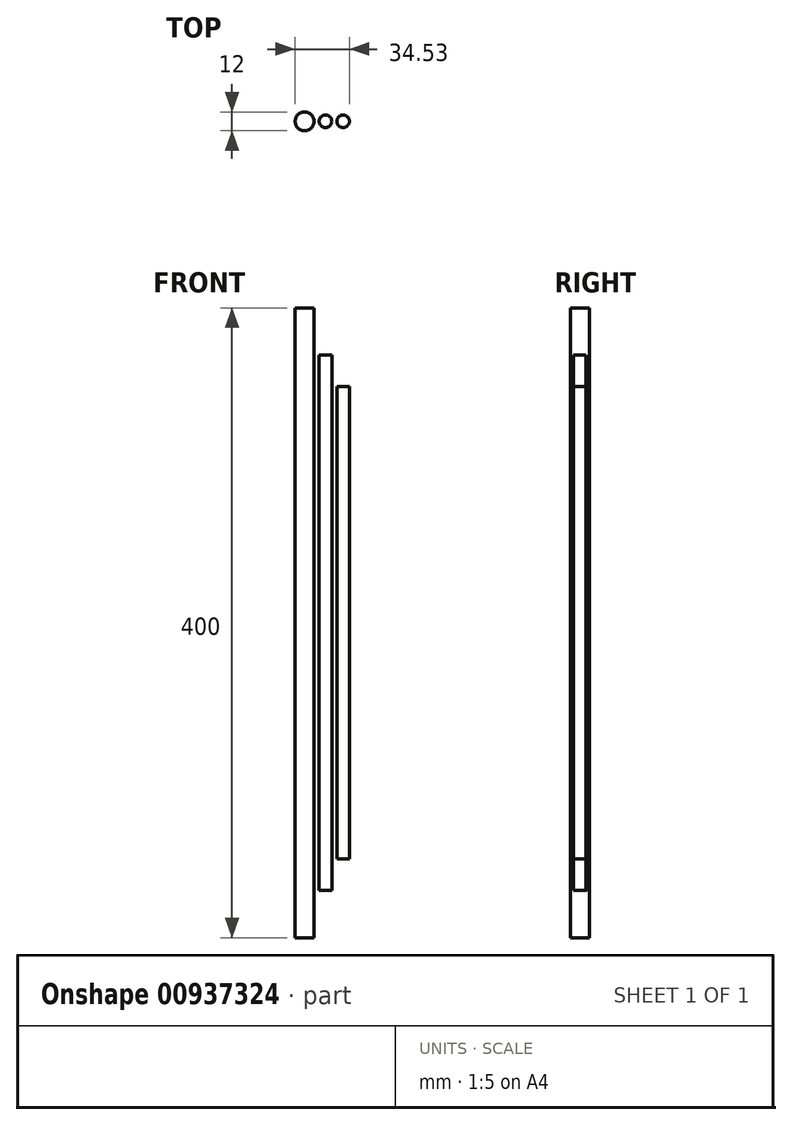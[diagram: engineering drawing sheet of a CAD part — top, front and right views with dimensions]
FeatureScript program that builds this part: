
annotation { "Feature Type Name" : "Feature", "Feature Type Description" : "" }
export const myFeature = defineFeature(function(context is Context, id is Id, definition is map)
    precondition{}
    {
        {
            var Q0;
            Q0=qCreatedBy(makeId("Top.planeOp"),FACE);
            var sketch = newSketch(context, id + "F0", { "sketchPlane" : qUnion([Q0])});
            skCircle(sketch, "E0", {"center": v(-13.3, 0) * mm, "radius": 6 * mm});
            skCircle(sketch, "E1", {"center": v(0, 0) * mm, "radius": 4 * mm});
            skCircle(sketch, "E2", {"center": v(11.23, 0) * mm, "radius": 4 * mm});
            skSolve(sketch);
        }
        {
            var Q0;
            Q0=makeQuery(id+"F0.imprint","IMPRINT",FACE,{"disambiguationData":[TD([[makeQuery(id+"F0.imprint","IMPRINT",EDGE,{"derivedFrom":sQuery(id+"F0.wireOp",EDGE,"E0")}),1.0]])]});
            extrude(context, id + "F1", {"entities" : qUnion([Q0]), "depth" : 400 * mm, "offsetDistance" : 25 * mm, "symmetric" : true});
        }
        {
            var Q0;
            Q0=makeQuery(id+"F0.imprint","IMPRINT",FACE,{"disambiguationData":[TD([[makeQuery(id+"F0.imprint","IMPRINT",EDGE,{"derivedFrom":sQuery(id+"F0.wireOp",EDGE,"E1")}),1.0]])]});
            extrude(context, id + "F2", {"entities" : qUnion([Q0]), "depth" : 340 * mm, "offsetDistance" : 25 * mm, "symmetric" : true});
        }
        {
            var Q0;
            Q0=makeQuery(id+"F0.imprint","IMPRINT",FACE,{"disambiguationData":[TD([[makeQuery(id+"F0.imprint","IMPRINT",EDGE,{"derivedFrom":sQuery(id+"F0.wireOp",EDGE,"E2")}),1.0]])]});
            extrude(context, id + "F3", {"entities" : qUnion([Q0]), "depth" : 300 * mm, "offsetDistance" : 25 * mm, "symmetric" : true});
        }
    });
